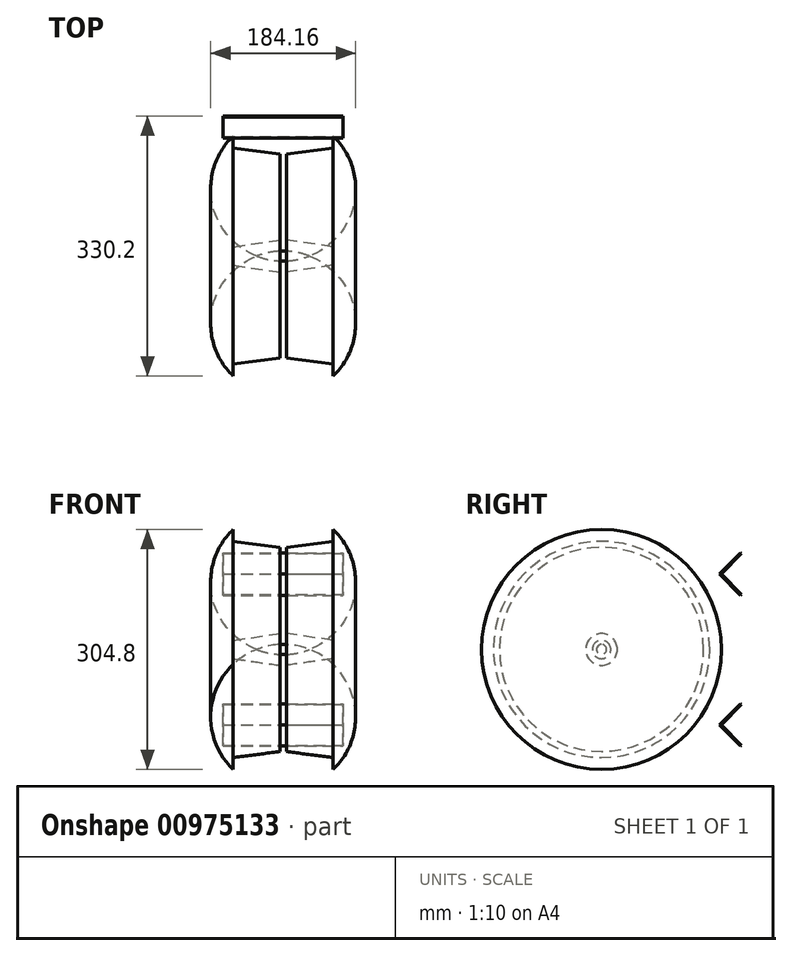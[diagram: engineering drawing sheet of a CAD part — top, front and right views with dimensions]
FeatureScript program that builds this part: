
annotation { "Feature Type Name" : "Feature", "Feature Type Description" : "" }
export const myFeature = defineFeature(function(context is Context, id is Id, definition is map)
    precondition{}
    {
        {
            var Q0;
            Q0=qCreatedBy(makeId("Top.planeOp"),FACE);
            var sketch = newSketch(context, id + "F0", { "sketchPlane" : qUnion([Q0])});
            skPoint(sketch, "E0.middle", {"position": v(0, 0) * mm});
            skLineSegment(sketch, "E1", {"start": v(0, 0) * mm, "end": v(0, 177.8) * mm, "construction": true});
            skPoint(sketch, "E1.endSnap0", {"position": v(0, 152.4) * mm});
            skArc(sketch, "E2", {"start": v(63.5, 152.4) * mm, "mid": v(0, 177.8) * mm, "end": v(-63.5, 152.4) * mm});
            skLineSegment(sketch, "E3", {"start": v(-63.5, 0) * mm, "end": v(-179.58, 0) * mm, "construction": true});
            skLineSegment(sketch, "E4", {"start": v(63.5, 0) * mm, "end": v(-63.5, 0) * mm});
            skLineSegment(sketch, "E5", {"start": v(63.5, 152.4) * mm, "end": v(63.5, 137.34) * mm});
            skLineSegment(sketch, "E6", {"start": v(63.5, 137.34) * mm, "end": v(4.12, 129.7) * mm});
            skLineSegment(sketch, "E7", {"start": v(4.12, 129.7) * mm, "end": v(4.12, 20.13) * mm});
            skLineSegment(sketch, "E8", {"start": v(4.12, 20.13) * mm, "end": v(63.5, 11.72) * mm});
            skLineSegment(sketch, "E9", {"start": v(63.5, 11.72) * mm, "end": v(63.5, 0) * mm});
            skLineSegment(sketch, "E10.MirrorCS", {"start": v(-63.5, 152.4) * mm, "end": v(-63.5, 137.34) * mm});
            skLineSegment(sketch, "E11.MirrorCS", {"start": v(-63.5, 137.34) * mm, "end": v(-4.12, 129.7) * mm});
            skLineSegment(sketch, "E12.MirrorCS", {"start": v(-4.12, 129.7) * mm, "end": v(-4.12, 20.13) * mm});
            skLineSegment(sketch, "E13.MirrorCS", {"start": v(-4.12, 20.13) * mm, "end": v(-63.5, 11.72) * mm});
            skLineSegment(sketch, "E14.MirrorCS", {"start": v(-63.5, 11.72) * mm, "end": v(-63.5, 0) * mm});
            skSolve(sketch);
        }
        {
            var Q0;
            Q0 = qSketchRegion(id + "F0", true);
            var Q1;
            Q1=sQuery(id+"F0.wireOp",EDGE,"E3");
            revolve(context, id + "F1", {"surfaceOperationType" : NewSurfaceOperationType.NEW, "entities" : qUnion([Q0]), "axis" : qUnion([Q1]), "revolveType" : RevolveType.FULL});
        }
        {
            var Q0;
            Q0=qCreatedBy(makeId("Right.planeOp"),FACE);
            cPlane(context, id + "F2", {"entities" : qUnion([Q0]), "cplaneType" : CPlaneType.OFFSET, "offset" : 76.2 * mm, "width" : 150 * mm, "height" : 150 * mm});
        }
        {
            var Q0;
            Q0=qCreatedBy(id+"F2.planeOp",FACE);
            var sketch = newSketch(context, id + "F3", { "sketchPlane" : qUnion([Q0])});
            skLineSegment(sketch, "E15", {"start": v(149.75, -95.86) * mm, "end": v(176.69, -122.8) * mm});
            skLineSegment(sketch, "E16", {"start": v(149.75, -95.86) * mm, "end": v(176.69, -95.86) * mm, "construction": true});
            skLineSegment(sketch, "E17", {"start": v(176.69, -95.86) * mm, "end": v(176.69, -122.8) * mm, "construction": true});
            skLineSegment(sketch, "E18", {"start": v(176.69, -122.8) * mm, "end": v(177.8, -121.69) * mm});
            skLineSegment(sketch, "E19", {"start": v(177.8, -121.69) * mm, "end": v(151.97, -95.86) * mm});
            skLineSegment(sketch, "E20.MirrorCS", {"start": v(177.8, -70.03) * mm, "end": v(151.97, -95.86) * mm});
            skLineSegment(sketch, "E21.MirrorCS", {"start": v(176.69, -68.92) * mm, "end": v(177.8, -70.03) * mm});
            skLineSegment(sketch, "E22.MirrorCS", {"start": v(149.75, -95.86) * mm, "end": v(176.69, -68.92) * mm});
            skArc(sketch, "E23", {"start": v(177.8, 0) * mm, "mid": v(144.94, -102.98) * mm, "end": v(58.5, -167.9) * mm, "construction": true});
            skLineSegment(sketch, "E24.MirrorCS", {"start": v(177.8, 70.03) * mm, "end": v(151.97, 95.86) * mm});
            skLineSegment(sketch, "E25.MirrorCS", {"start": v(149.75, 95.86) * mm, "end": v(176.69, 68.92) * mm});
            skLineSegment(sketch, "E26.MirrorCS", {"start": v(176.69, 68.92) * mm, "end": v(177.8, 70.03) * mm});
            skLineSegment(sketch, "E27.MirrorCS", {"start": v(177.8, 121.69) * mm, "end": v(151.97, 95.86) * mm});
            skLineSegment(sketch, "E28.MirrorCS", {"start": v(149.75, 95.86) * mm, "end": v(176.69, 122.8) * mm});
            skLineSegment(sketch, "E29.MirrorCS", {"start": v(176.69, 122.8) * mm, "end": v(177.8, 121.69) * mm});
            skSolve(sketch);
        }
        {
            var Q0;
            Q0 = qSketchRegion(id + "F3", true);
            extrude(context, id + "F4", {"entities" : qUnion([Q0]), "depth" : -152.4 * mm, "offsetDistance" : 25 * mm});
        }
    });
